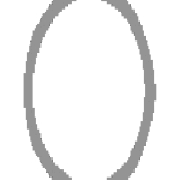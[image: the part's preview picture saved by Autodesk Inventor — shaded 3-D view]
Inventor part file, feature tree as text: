
AUTODESK INVENTOR PART (.ipt)
format: ipt  version: 2021 (Build 250183000, 183)  size: 110,080 bytes
history: native  units: in
note: dims shown in document units (in); Inventor stores cm internally (conversion verified against a paired STEP export)
features: other x4, sketch x3, plane x1
ambient origin geometry x8: Origin, YZ Plane, XZ Plane, XY Plane, X Axis, Y Axis, Z Axis, Center Point
bodies: Solid1 (feature_tree), Body (feature_tree)
feature tree (8):
  other  "Driven Length"
  other  "Frame Generator"
  other  "Start Plane"
  other  "End Plane"
  sketch  "Sketch"  dims[d2=11.5in d4=-0.0in d5=11.5in d6=0.12in d7=0.0in d8=90.0deg d9=11.5in]
  sketch  "Sketch2"  dims[d0=1.0in]
  plane  "Work Plane3"
  sketch  "Sketch3"  dims[d1=0.065in]
